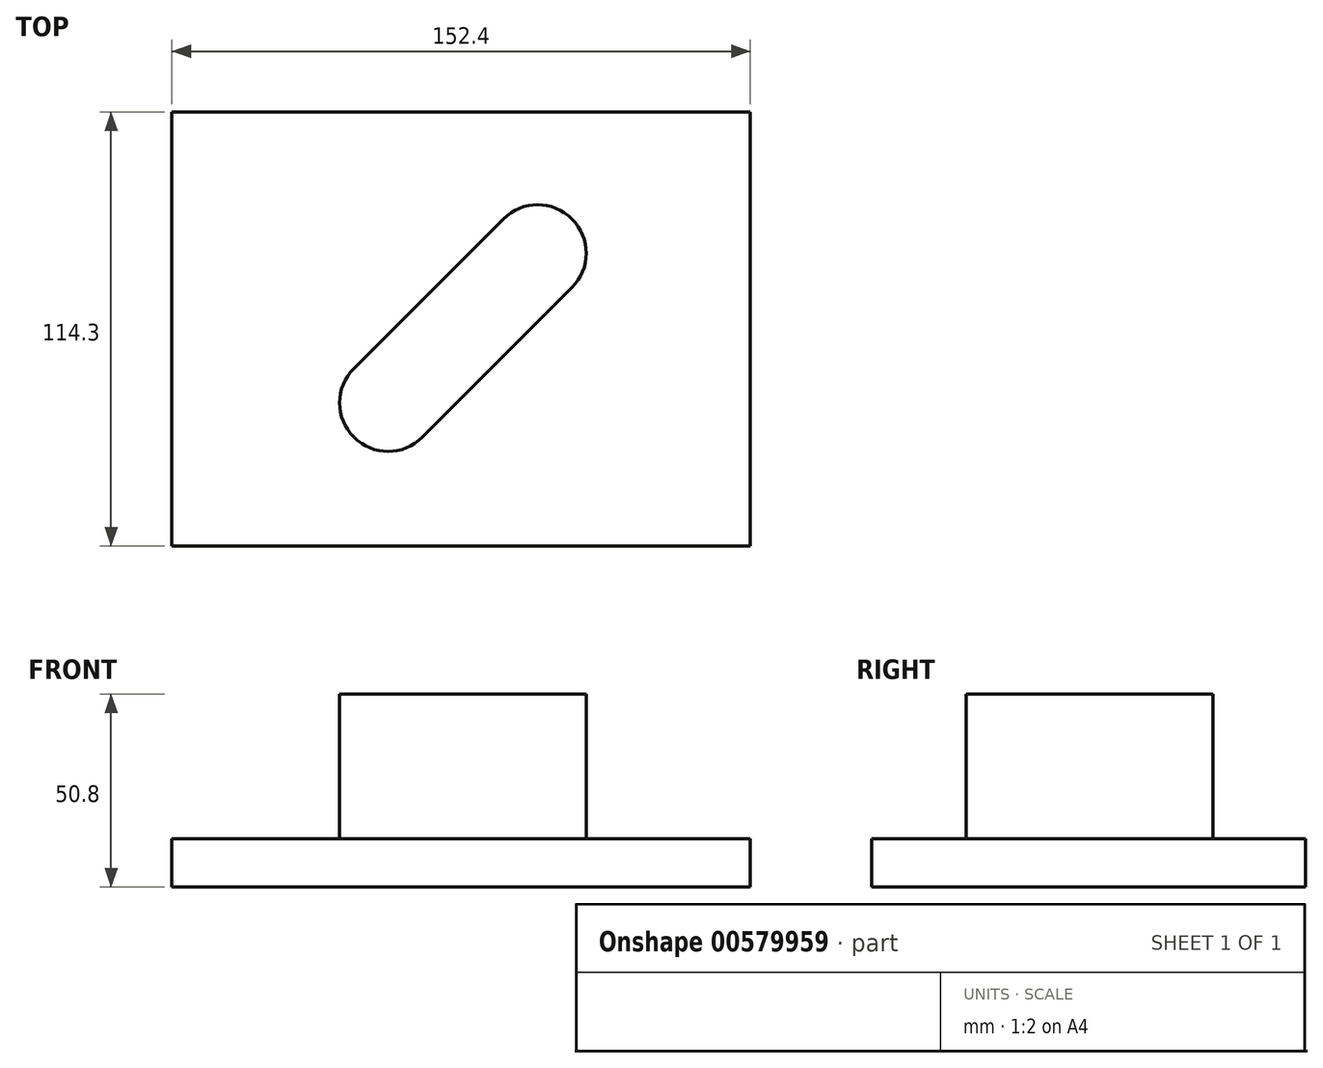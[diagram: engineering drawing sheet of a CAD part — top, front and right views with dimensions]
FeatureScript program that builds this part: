
annotation { "Feature Type Name" : "Feature", "Feature Type Description" : "" }
export const myFeature = defineFeature(function(context is Context, id is Id, definition is map)
    precondition{}
    {
        {
            var Q0;
            Q0=qCreatedBy(makeId("Top.planeOp"),FACE);
            var sketch = newSketch(context, id + "F0", { "sketchPlane" : qUnion([Q0])});
            skLineSegment(sketch, "E0.bottom", {"start": v(-76.2, -57.05) * mm, "end": v(76.2, -57.05) * mm});
            skLineSegment(sketch, "E0.top", {"start": v(-76.2, 57.25) * mm, "end": v(76.2, 57.25) * mm});
            skLineSegment(sketch, "E0.left", {"start": v(-76.2, -57.05) * mm, "end": v(-76.2, 57.25) * mm});
            skLineSegment(sketch, "E0.right", {"start": v(76.2, -57.05) * mm, "end": v(76.2, 57.25) * mm});
            skLineSegment(sketch, "E1", {"start": v(0, 57.25) * mm, "end": v(0, -57.05) * mm, "construction": true});
            skLineSegment(sketch, "E2", {"start": v(-76.2, 0) * mm, "end": v(0, 0) * mm, "construction": true});
            skLineSegment(sketch, "E3", {"start": v(0, 0) * mm, "end": v(-8.98, 8.98) * mm});
            skLineSegment(sketch, "E4", {"start": v(-8.98, 8.98) * mm, "end": v(0, 0) * mm, "construction": true});
            skLineSegment(sketch, "E5.1.0", {"start": v(9.1, -9.1) * mm, "end": v(0.12, -0.12) * mm, "construction": true});
            skPoint(sketch, "E5.center", {"position": v(0.06, -0.06) * mm});
            skLineSegment(sketch, "E6", {"start": v(-8.98, 8.98) * mm, "end": v(11.13, 29.09) * mm});
            skLineSegment(sketch, "E7", {"start": v(9.1, -9.1) * mm, "end": v(29.21, 11) * mm});
            skLineSegment(sketch, "E8", {"start": v(-8.98, 8.98) * mm, "end": v(-28.26, -10.3) * mm});
            skLineSegment(sketch, "E9", {"start": v(9.1, -9.1) * mm, "end": v(-10.18, -28.38) * mm});
            skArc(sketch, "E10", {"start": v(29.21, 11) * mm, "mid": v(29.21, 29.09) * mm, "end": v(11.13, 29.09) * mm});
            skArc(sketch, "E11", {"start": v(-28.26, -10.3) * mm, "mid": v(-28.26, -28.38) * mm, "end": v(-10.18, -28.38) * mm});
            skLineSegment(sketch, "E12", {"start": v(-28.26, -10.3) * mm, "end": v(-10.18, -28.38) * mm, "construction": true});
            skLineSegment(sketch, "E13", {"start": v(11.13, 29.09) * mm, "end": v(29.21, 11) * mm, "construction": true});
            skSolve(sketch);
        }
        {
            var Q0;
            Q0=makeQuery(id+"F0.imprint","IMPRINT",FACE,{"disambiguationData":[TD([[makeQuery(id+"F0.imprint","IMPRINT",EDGE,{"derivedFrom":sQuery(id+"F0.wireOp",EDGE,"E0.bottom")}),1.0]])]});
            var Q1;
            Q1=makeQuery(id+"F0.imprint","IMPRINT",FACE,{"disambiguationData":[TD([[makeQuery(id+"F0.imprint","IMPRINT",EDGE,{"derivedFrom":sQuery(id+"F0.wireOp",EDGE,"E6")}),-1.0]])]});
            extrude(context, id + "F1", {"entities" : qUnion([Q0, Q1]), "depth" : 12.7 * mm, "offsetDistance" : 25.4 * mm});
        }
        {
            var Q0;
            Q0=makeQuery(id+"F0.imprint","IMPRINT",FACE,{"disambiguationData":[TD([[makeQuery(id+"F0.imprint","IMPRINT",EDGE,{"derivedFrom":sQuery(id+"F0.wireOp",EDGE,"E6")}),-1.0]])]});
            extrude(context, id + "F2", {"entities" : qUnion([Q0]), "operationType" : NewBodyOperationType.ADD, "depth" : 50.8 * mm, "offsetDistance" : 25.4 * mm});
        }
    });
